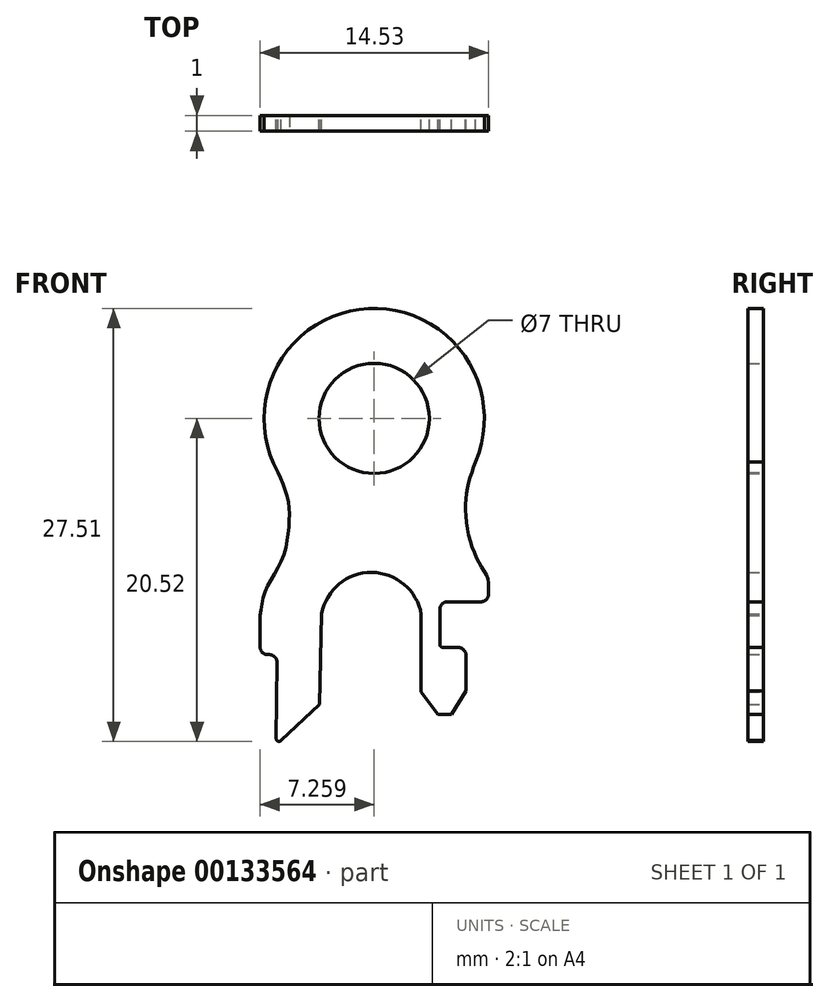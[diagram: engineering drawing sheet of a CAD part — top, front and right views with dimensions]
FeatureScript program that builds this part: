
annotation { "Feature Type Name" : "Feature", "Feature Type Description" : "" }
export const myFeature = defineFeature(function(context is Context, id is Id, definition is map)
    precondition{}
    {
        {
            var Q0;
            Q0=qCreatedBy(makeId("Front.planeOp"),FACE);
            var sketch = newSketch(context, id + "F0", { "sketchPlane" : qUnion([Q0])});
            skLineSegment(sketch, "E0", {"start": v(-4.18, -15.4) * mm, "end": v(-4.04, -9.66) * mm});
            skLineSegment(sketch, "E1", {"start": v(2.28, -9.7) * mm, "end": v(2.28, -14.62) * mm});
            skLineSegment(sketch, "E2", {"start": v(2.28, -14.62) * mm, "end": v(3.36, -16.05) * mm});
            skLineSegment(sketch, "E3", {"start": v(3.36, -16.05) * mm, "end": v(4.21, -16.05) * mm});
            skLineSegment(sketch, "E4", {"start": v(4.21, -16.05) * mm, "end": v(5.12, -14.56) * mm});
            skLineSegment(sketch, "E5", {"start": v(5.12, -14.56) * mm, "end": v(5.12, -12.29) * mm});
            skLineSegment(sketch, "E6", {"start": v(4.62, -11.79) * mm, "end": v(3.66, -11.79) * mm});
            skLineSegment(sketch, "E7", {"start": v(3.46, -11.59) * mm, "end": v(3.46, -9.4) * mm});
            skLineSegment(sketch, "E8", {"start": v(3.96, -8.9) * mm, "end": v(6.07, -8.9) * mm});
            skLineSegment(sketch, "E9", {"start": v(6.57, -8.4) * mm, "end": v(6.57, -7.7) * mm});
            skLineSegment(sketch, "E10", {"start": v(-7.96, -9.77) * mm, "end": v(-7.96, -11.75) * mm});
            skArc(sketch, "E11", {"start": v(2.28, -9.7) * mm, "mid": v(-0.86, -7.02) * mm, "end": v(-4.04, -9.66) * mm});
            skCircle(sketch, "E12", {"center": v(-0.7, 2.76) * mm, "radius": 3.5 * mm});
            skFitSpline(sketch, "E13", {"points": [v(6.57, -7.7) * mm, v(6.17, -6.75) * mm, v(5.48, -5.3) * mm, v(5.1, -3.2) * mm, v(5.25, -1.56) * mm, v(5.73, 0) * mm], "startDerivative": vector(0, 6.3) * mm, "endDerivative": vector(2.74, 7.68) * mm});
            skFitSpline(sketch, "E14", {"points": [v(-7.96, -9.77) * mm, v(-7.59, -8.16) * mm, v(-6.57, -6.23) * mm, v(-6.12, -4.08) * mm, v(-6.2, -2.35) * mm, v(-6.82, -0.66) * mm], "startDerivative": vector(1.24, 8.6) * mm, "endDerivative": vector(-3.83, 8.66) * mm});
            skPoint(sketch, "E15.visualSharp", {"position": v(6.57, -8.9) * mm});
            skArc(sketch, "E15.filletArc", {"start": v(6.07, -8.9) * mm, "mid": v(6.42, -8.75) * mm, "end": v(6.57, -8.4) * mm});
            skPoint(sketch, "E16.visualSharp", {"position": v(3.46, -8.9) * mm});
            skArc(sketch, "E16.filletArc", {"start": v(3.96, -8.9) * mm, "mid": v(3.6, -9.04) * mm, "end": v(3.46, -9.4) * mm});
            skPoint(sketch, "E17.visualSharp", {"position": v(5.12, -11.79) * mm});
            skArc(sketch, "E17.filletArc", {"start": v(5.12, -12.29) * mm, "mid": v(4.98, -11.93) * mm, "end": v(4.62, -11.79) * mm});
            skLineSegment(sketch, "E18", {"start": v(-4.18, -15.4) * mm, "end": v(-6.61, -17.7) * mm});
            skLineSegment(sketch, "E19", {"start": v(-7.46, -12.25) * mm, "end": v(-7.37, -12.25) * mm});
            skLineSegment(sketch, "E20", {"start": v(-6.87, -12.75) * mm, "end": v(-6.92, -17.58) * mm});
            skPoint(sketch, "E21.visualSharp", {"position": v(-7.96, -12.25) * mm});
            skArc(sketch, "E21.filletArc", {"start": v(-7.96, -11.75) * mm, "mid": v(-7.81, -12.1) * mm, "end": v(-7.46, -12.25) * mm});
            skPoint(sketch, "E22.visualSharp", {"position": v(-6.86, -12.25) * mm});
            skArc(sketch, "E22.filletArc", {"start": v(-6.87, -12.75) * mm, "mid": v(-7.01, -12.4) * mm, "end": v(-7.37, -12.25) * mm});
            skArc(sketch, "E23", {"start": v(-6.92, -17.58) * mm, "mid": v(-6.81, -17.75) * mm, "end": v(-6.61, -17.7) * mm});
            skPoint(sketch, "E24.visualSharp", {"position": v(3.46, -11.79) * mm});
            skArc(sketch, "E24.filletArc", {"start": v(3.46, -11.59) * mm, "mid": v(3.52, -11.73) * mm, "end": v(3.66, -11.79) * mm});
            skArc(sketch, "E25", {"start": v(5.73, 0) * mm, "mid": v(-1.08, 9.74) * mm, "end": v(-6.82, -0.66) * mm});
            skSolve(sketch);
        }
        {
            var Q0;
            Q0=makeQuery(id+"F0.imprint","IMPRINT",FACE,{"disambiguationData":[TD([[makeQuery(id+"F0.imprint","IMPRINT",EDGE,{"derivedFrom":sQuery(id+"F0.wireOp",EDGE,"E12")}),-1.0]])]});
            var Q1;
            Q1=makeQuery(id+"F0.imprint","IMPRINT",FACE,{"disambiguationData":[TD([[makeQuery(id+"F0.imprint","IMPRINT",EDGE,{"derivedFrom":sQuery(id+"F0.wireOp",EDGE,"E0")}),1.0]])]});
            extrude(context, id + "F1", {"entities" : qUnion([Q0, Q1]), "depth" : 1 * mm});
        }
    });
